# Revit family: Fire-Extinguisher-Cabinet
name_source: partatom
category: Specialty Equipment
units: mm (PartAtom-declared; Revit-internal decimal feet)

## family parameters
Always vertical = Yes
Classification Number = 23.65.70.17.11.27
Cut with Voids When Loaded = No
Enable Cutting in Views = No
Maintain Annotation Orientation = No
Part Type = Normal
Room Calculation Point = No
Round Connector Dimension = Use Diameter
Shared = No
Work Plane-Based = No

## types (1)
- Fire-Extinguisher-Cabinet
    Assembly Code = D4030200
    Cabinet Material = Metal - Steel, Painted, Red
    Cabinet Trim Material = Metal - Steel, Painted, White
    Construction Details = http://www.arcat.com
    Default Elevation = 0' - 0"
    Depth = 0' - 6 1/2"
    Description = Fire Extinguisher Cabinet
    Expected Lifespan (Years) = 15
    Fire Rating = 1 Hour
    Glazing Material = Glass, Tempered, 1/8"
    Green Building-LEED = http://www.arcat.com
    Height = 2' - 1"
    Keynote = 10522
    Maintenance Schedule (Months) = 6
    Manufacturer = Generic
    Manufacturer Fax = (203) 939-2444
    Manufacturer Website = http://www.arcat.com
    Model = Generic
    Product Data = http://www.arcat.com
    Product Properties = http://www.arcat.com
    Specification = http://www.arcat.com
    Warranty Duration (Years) = 1
    Width = 0' - 11 1/2"

## geometry (parser evidence)
native form markers: Sweep x2
no freeform markers — native parametric forms only
